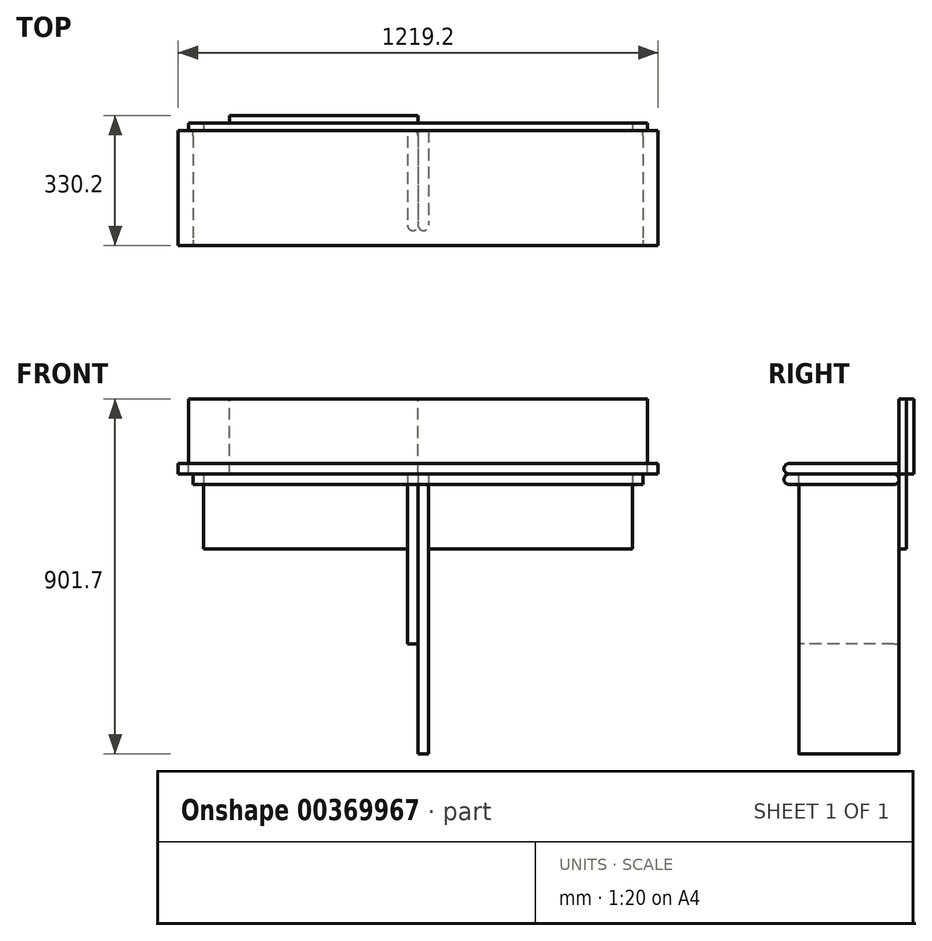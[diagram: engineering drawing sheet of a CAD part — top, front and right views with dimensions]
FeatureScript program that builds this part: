
annotation { "Feature Type Name" : "Feature", "Feature Type Description" : "" }
export const myFeature = defineFeature(function(context is Context, id is Id, definition is map)
    precondition{}
    {
        {
            var Q0;
            Q0=qCreatedBy(makeId("Top.planeOp"),FACE);
            var sketch = newSketch(context, id + "F0", { "sketchPlane" : qUnion([Q0])});
            skLineSegment(sketch, "E0.bottom", {"start": v(-609.6, 0) * mm, "end": v(609.6, 0) * mm});
            skLineSegment(sketch, "E0.top", {"start": v(-609.6, -292.1) * mm, "end": v(609.6, -292.1) * mm});
            skLineSegment(sketch, "E0.left", {"start": v(-609.6, -292.1) * mm, "end": v(-609.6, 0) * mm});
            skLineSegment(sketch, "E0.right", {"start": v(609.6, -292.1) * mm, "end": v(609.6, 0) * mm});
            skSolve(sketch);
        }
        {
            var Q0;
            Q0 = qSketchRegion(id + "F0", true);
            extrude(context, id + "F1", {"entities" : qUnion([Q0]), "depth" : 26.92 * mm});
        }
        {
            var Q0;
            Q0=makeQuery(id+"F1.opExtrude","CAP_EDGE",EDGE,{"disambiguationData":[OSD([sQuery(id+"F0.wireOp",EDGE,"E0.top")])],"isStart":false});
            var Q1;
            Q1=makeQuery(id+"F1.opExtrude","CAP_EDGE",EDGE,{"disambiguationData":[OSD([sQuery(id+"F0.wireOp",EDGE,"E0.top")])],"isStart":true});
            fillet(context, id + "F2", {"entities" : qUnion([Q0, Q1]), "radius" : 13.46 * mm, "tangentPropagation" : true, "allowEdgeOverflow" : false});
        }
        {
            var Q0;
            Q0=qCreatedBy(makeId("Front.planeOp"),FACE);
            var sketch = newSketch(context, id + "F3", { "sketchPlane" : qUnion([Q0])});
            skLineSegment(sketch, "E1.bottom", {"start": v(-582.68, 0) * mm, "end": v(582.68, 0) * mm});
            skLineSegment(sketch, "E1.top", {"start": v(-582.68, 190.5) * mm, "end": v(582.68, 190.5) * mm});
            skLineSegment(sketch, "E1.left", {"start": v(-582.68, 0) * mm, "end": v(-582.68, 190.5) * mm});
            skLineSegment(sketch, "E1.right", {"start": v(582.68, 0) * mm, "end": v(582.68, 190.5) * mm});
            skSolve(sketch);
        }
        {
            var Q0;
            Q0=makeQuery(id+"F3.imprint","IMPRINT",FACE,{"disambiguationData":[TD([[makeQuery(id+"F3.imprint","IMPRINT",EDGE,{"derivedFrom":sQuery(id+"F3.wireOp",EDGE,"E1.bottom")}),1.0]])]});
            extrude(context, id + "F4", {"entities" : qUnion([Q0]), "oppositeDirection" : true, "depth" : 19.05 * mm});
        }
        {
            var Q0;
            Q0=qCreatedBy(makeId("Right.planeOp"),FACE);
            var sketch = newSketch(context, id + "F5", { "sketchPlane" : qUnion([Q0])});
            skLineSegment(sketch, "E2.bottom", {"start": v(0, 0) * mm, "end": v(-254, 0) * mm});
            skLineSegment(sketch, "E2.top", {"start": v(0, -711.2) * mm, "end": v(-254, -711.2) * mm});
            skLineSegment(sketch, "E2.left", {"start": v(0, 0) * mm, "end": v(0, -711.2) * mm});
            skLineSegment(sketch, "E2.right", {"start": v(-254, 0) * mm, "end": v(-254, -711.2) * mm});
            skSolve(sketch);
        }
        {
            var Q0;
            Q0=makeQuery(id+"F5.imprint","IMPRINT",FACE,{"disambiguationData":[TD([[makeQuery(id+"F5.imprint","IMPRINT",EDGE,{"derivedFrom":sQuery(id+"F5.wireOp",EDGE,"E2.bottom")}),1.0]])]});
            extrude(context, id + "F6", {"entities" : qUnion([Q0]), "depth" : 26.92 * mm});
        }
        {
            var Q0;
            Q0=qCreatedBy(makeId("Right.planeOp"),FACE);
            var sketch = newSketch(context, id + "F7", { "sketchPlane" : qUnion([Q0])});
            skLineSegment(sketch, "E3.bottom", {"start": v(0, 0) * mm, "end": v(-254, 0) * mm});
            skLineSegment(sketch, "E3.top", {"start": v(0, -431.8) * mm, "end": v(-254, -431.8) * mm});
            skLineSegment(sketch, "E3.left", {"start": v(0, 0) * mm, "end": v(0, -431.8) * mm});
            skLineSegment(sketch, "E3.right", {"start": v(-254, 0) * mm, "end": v(-254, -431.8) * mm});
            skSolve(sketch);
        }
        {
            var Q0;
            Q0=makeQuery(id+"F7.imprint","IMPRINT",FACE,{"disambiguationData":[TD([[makeQuery(id+"F7.imprint","IMPRINT",EDGE,{"derivedFrom":sQuery(id+"F7.wireOp",EDGE,"E3.bottom")}),1.0]])]});
            extrude(context, id + "F8", {"entities" : qUnion([Q0]), "oppositeDirection" : true, "depth" : 26.92 * mm});
        }
        {
            var Q0;
            Q0=makeQuery(id+"F6.opExtrude","CAP_EDGE",EDGE,{"disambiguationData":[OSD([sQuery(id+"F5.wireOp",EDGE,"E2.right")])],"isStart":true});
            var Q1;
            Q1=makeQuery(id+"F6.opExtrude","CAP_EDGE",EDGE,{"disambiguationData":[OSD([sQuery(id+"F5.wireOp",EDGE,"E2.right")])],"isStart":false});
            fillet(context, id + "F9", {"entities" : qUnion([Q0, Q1]), "radius" : 13.46 * mm, "allowEdgeOverflow" : false});
        }
        {
            var Q0;
            Q0=makeQuery(id+"F8.opExtrude","CAP_EDGE",EDGE,{"disambiguationData":[OSD([sQuery(id+"F7.wireOp",EDGE,"E3.right")])],"isStart":false});
            var Q1;
            Q1=makeQuery(id+"F8.opExtrude","CAP_EDGE",EDGE,{"disambiguationData":[OSD([sQuery(id+"F7.wireOp",EDGE,"E3.right")])],"isStart":true});
            var Q2;
            Q2=makeQuery(id+"F8.opExtrude","CAP_EDGE",EDGE,{"disambiguationData":[OSD([sQuery(id+"F7.wireOp",EDGE,"E3.left")])],"isStart":false});
            var Q3;
            Q3=makeQuery(id+"F8.opExtrude","CAP_EDGE",EDGE,{"disambiguationData":[OSD([sQuery(id+"F7.wireOp",EDGE,"E3.left")])],"isStart":true});
            fillet(context, id + "F10", {"entities" : qUnion([Q0, Q1, Q2, Q3]), "radius" : 13.46 * mm, "tangentPropagation" : true, "allowEdgeOverflow" : false});
        }
        {
            var Q0;
            Q0=qCreatedBy(makeId("Top.planeOp"),FACE);
            var sketch = newSketch(context, id + "F11", { "sketchPlane" : qUnion([Q0])});
            skLineSegment(sketch, "E4.bottom", {"start": v(-571.5, 0) * mm, "end": v(571.5, 0) * mm});
            skLineSegment(sketch, "E4.top", {"start": v(-571.5, -292.1) * mm, "end": v(571.5, -292.1) * mm});
            skLineSegment(sketch, "E4.left", {"start": v(-571.5, 0) * mm, "end": v(-571.5, -292.1) * mm});
            skLineSegment(sketch, "E4.right", {"start": v(571.5, 0) * mm, "end": v(571.5, -292.1) * mm});
            skSolve(sketch);
        }
        {
            var Q0;
            Q0 = qSketchRegion(id + "F11", true);
            extrude(context, id + "F12", {"entities" : qUnion([Q0]), "oppositeDirection" : true, "depth" : 26.92 * mm});
        }
        {
            var Q0;
            Q0=makeQuery(id+"F12.opExtrude","CAP_EDGE",EDGE,{"disambiguationData":[OSD([sQuery(id+"F11.wireOp",EDGE,"E4.top")])],"isStart":true});
            var Q1;
            Q1=makeQuery(id+"F12.opExtrude","CAP_EDGE",EDGE,{"disambiguationData":[OSD([sQuery(id+"F11.wireOp",EDGE,"E4.top")])],"isStart":false});
            var Q2;
            Q2=makeQuery(id+"F12.opExtrude","CAP_EDGE",EDGE,{"disambiguationData":[OSD([sQuery(id+"F11.wireOp",EDGE,"E4.bottom")])],"isStart":false});
            var Q3;
            Q3=makeQuery(id+"F12.opExtrude","CAP_EDGE",EDGE,{"disambiguationData":[OSD([sQuery(id+"F11.wireOp",EDGE,"E4.bottom")])],"isStart":true});
            fillet(context, id + "F13", {"entities" : qUnion([Q0, Q1, Q2, Q3]), "radius" : 13.46 * mm, "tangentPropagation" : true, "allowEdgeOverflow" : false});
        }
        {
            var Q0;
            Q0=qCreatedBy(makeId("Front.planeOp"),FACE);
            var sketch = newSketch(context, id + "F14", { "sketchPlane" : qUnion([Q0])});
            skLineSegment(sketch, "E5.bottom", {"start": v(-544.58, 0) * mm, "end": v(544.58, 0) * mm});
            skLineSegment(sketch, "E5.top", {"start": v(-544.58, -190.5) * mm, "end": v(544.58, -190.5) * mm});
            skLineSegment(sketch, "E5.left", {"start": v(-544.58, 0) * mm, "end": v(-544.58, -190.5) * mm});
            skLineSegment(sketch, "E5.right", {"start": v(544.58, 0) * mm, "end": v(544.58, -190.5) * mm});
            skSolve(sketch);
        }
        {
            var Q0;
            Q0=makeQuery(id+"F14.imprint","IMPRINT",FACE,{"disambiguationData":[TD([[makeQuery(id+"F14.imprint","IMPRINT",EDGE,{"derivedFrom":sQuery(id+"F14.wireOp",EDGE,"E5.bottom")}),-1.0]])]});
            extrude(context, id + "F15", {"entities" : qUnion([Q0]), "oppositeDirection" : true, "depth" : 19.05 * mm});
        }
        {
            var Q0;
            Q0=makeQuery(id+"F4.opExtrude","CAP_FACE",FACE,{"disambiguationData":[OSD([sQuery(id+"F3.wireOp",EDGE,"E1.bottom"),sQuery(id+"F3.wireOp",EDGE,"E1.top"),sQuery(id+"F3.wireOp",EDGE,"E1.left"),sQuery(id+"F3.wireOp",EDGE,"E1.right")])],"isStart":false});
            var sketch = newSketch(context, id + "F16", { "sketchPlane" : qUnion([Q0])});
            skLineSegment(sketch, "E6.bottom", {"start": v(0, 0) * mm, "end": v(479.55, 0) * mm});
            skLineSegment(sketch, "E6.top", {"start": v(0, 190.5) * mm, "end": v(479.55, 190.5) * mm});
            skLineSegment(sketch, "E6.left", {"start": v(0, 0) * mm, "end": v(0, 190.5) * mm});
            skLineSegment(sketch, "E6.right", {"start": v(479.55, 0) * mm, "end": v(479.55, 190.5) * mm});
            skSolve(sketch);
        }
        {
            var Q0;
            Q0 = qSketchRegion(id + "F16", true);
            extrude(context, id + "F17", {"entities" : qUnion([Q0]), "depth" : 19.05 * mm});
        }
    });
